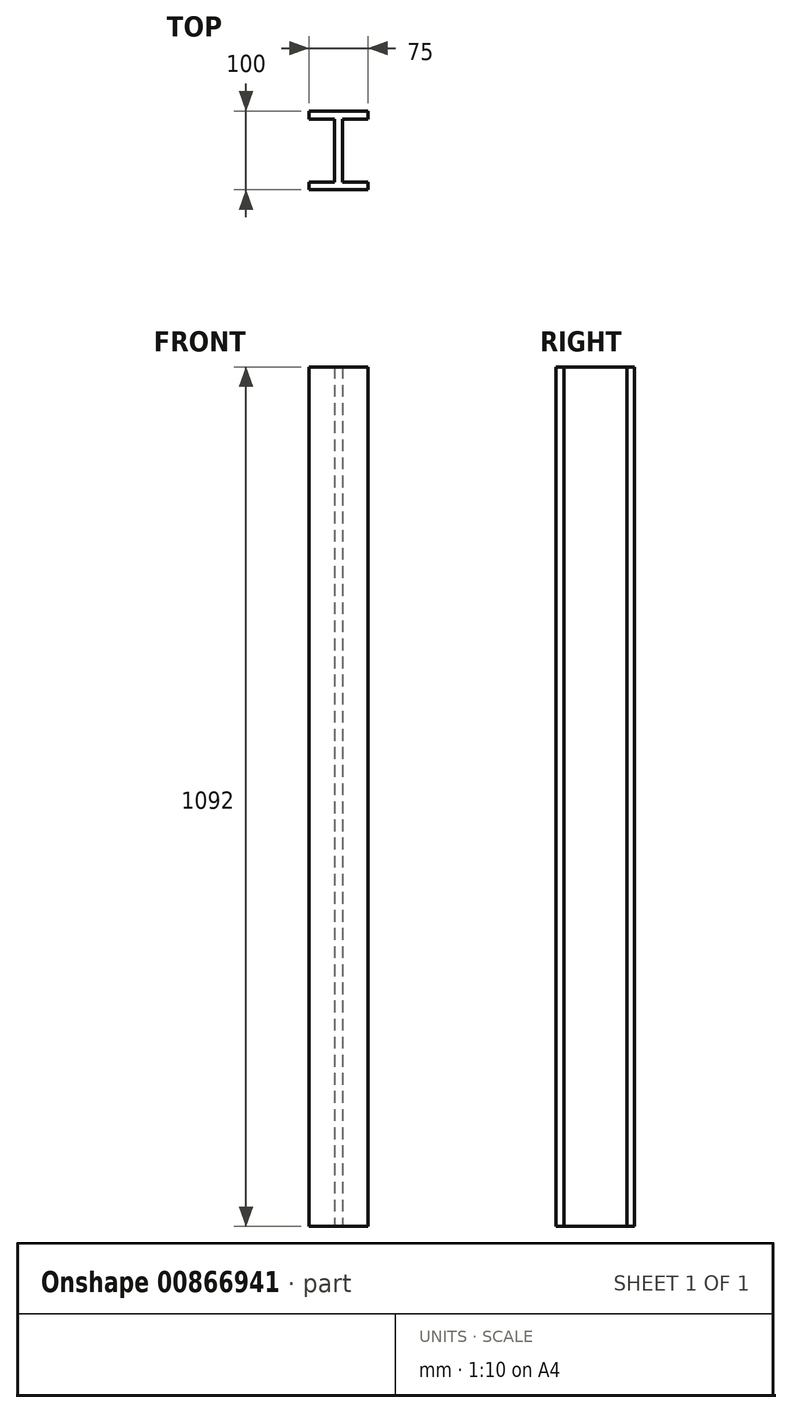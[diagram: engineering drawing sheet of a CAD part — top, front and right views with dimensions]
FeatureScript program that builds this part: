
annotation { "Feature Type Name" : "Feature", "Feature Type Description" : "" }
export const myFeature = defineFeature(function(context is Context, id is Id, definition is map)
    precondition{}
    {
        {
            var Q0;
            Q0=qCreatedBy(makeId("Top.planeOp"),FACE);
            var sketch = newSketch(context, id + "F0", { "sketchPlane" : qUnion([Q0])});
            skLineSegment(sketch, "E0", {"start": v(0, -50) * mm, "end": v(37.5, -50) * mm});
            skLineSegment(sketch, "E1", {"start": v(37.5, -50) * mm, "end": v(37.5, -40) * mm});
            skLineSegment(sketch, "E2", {"start": v(37.5, -40) * mm, "end": v(5, -40) * mm});
            skLineSegment(sketch, "E3", {"start": v(5, -40) * mm, "end": v(5, 0) * mm});
            skLineSegment(sketch, "E4", {"start": v(0, -91.84) * mm, "end": v(0, 94.64) * mm, "construction": true});
            skLineSegment(sketch, "E5", {"start": v(108.7, 0) * mm, "end": v(-118.34, 0) * mm, "construction": true});
            skLineSegment(sketch, "E6.MirrorCS", {"start": v(-5, -40) * mm, "end": v(-5, 0) * mm});
            skLineSegment(sketch, "E7.MirrorCS", {"start": v(-37.5, -40) * mm, "end": v(-5, -40) * mm});
            skLineSegment(sketch, "E8.MirrorCS", {"start": v(-37.5, -50) * mm, "end": v(-37.5, -40) * mm});
            skLineSegment(sketch, "E9.MirrorCS", {"start": v(0, -50) * mm, "end": v(-37.5, -50) * mm});
            skLineSegment(sketch, "E10.MirrorCS", {"start": v(-5, 40) * mm, "end": v(-5, 0) * mm});
            skLineSegment(sketch, "E11.MirrorCS", {"start": v(-37.5, 40) * mm, "end": v(-5, 40) * mm});
            skLineSegment(sketch, "E12.MirrorCS", {"start": v(0, 50) * mm, "end": v(-37.5, 50) * mm});
            skLineSegment(sketch, "E13.MirrorCS", {"start": v(-37.5, 50) * mm, "end": v(-37.5, 40) * mm});
            skLineSegment(sketch, "E14.MirrorCS", {"start": v(37.5, 50) * mm, "end": v(37.5, 40) * mm});
            skLineSegment(sketch, "E15.MirrorCS", {"start": v(0, 50) * mm, "end": v(37.5, 50) * mm});
            skLineSegment(sketch, "E16.MirrorCS", {"start": v(37.5, 40) * mm, "end": v(5, 40) * mm});
            skLineSegment(sketch, "E17.MirrorCS", {"start": v(5, 40) * mm, "end": v(5, 0) * mm});
            skSolve(sketch);
        }
        {
            var Q0;
            Q0 = qSketchRegion(id + "F0", true);
            extrude(context, id + "F1", {"entities" : qUnion([Q0]), "depth" : 1092 * mm, "offsetDistance" : 25 * mm});
        }
    });
